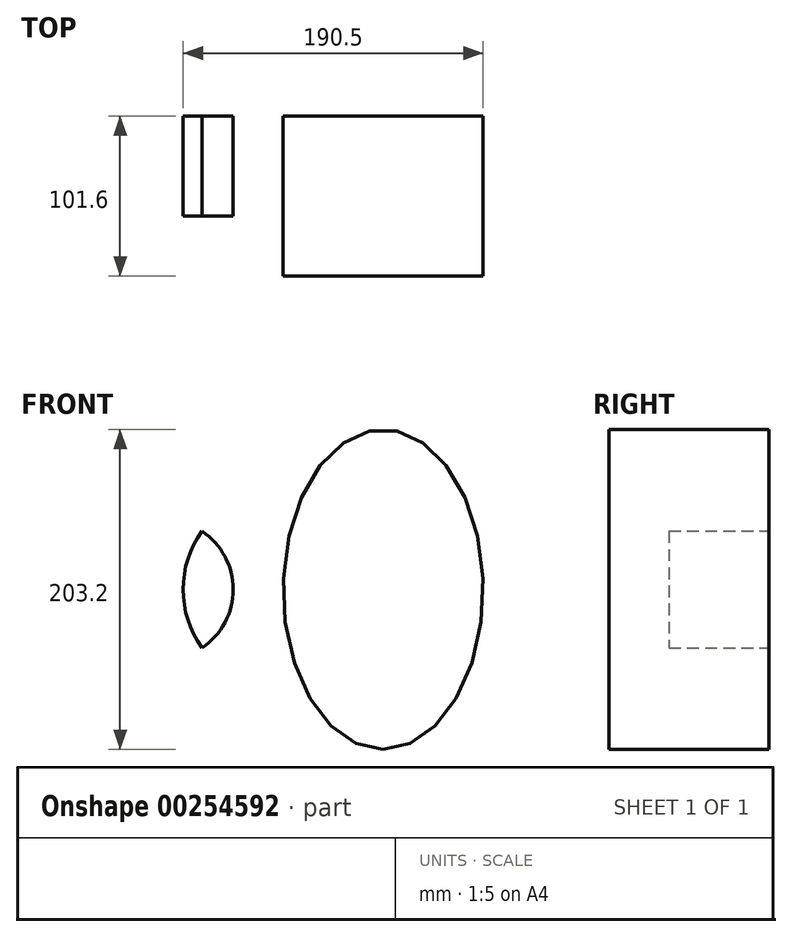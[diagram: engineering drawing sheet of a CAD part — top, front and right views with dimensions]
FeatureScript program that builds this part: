
annotation { "Feature Type Name" : "Feature", "Feature Type Description" : "" }
export const myFeature = defineFeature(function(context is Context, id is Id, definition is map)
    precondition{}
    {
        {
            var Q0;
            Q0=qCreatedBy(makeId("Front.planeOp"),FACE);
            var sketch = newSketch(context, id + "F0", { "sketchPlane" : qUnion([Q0])});
            skLineSegment(sketch, "E0", {"start": v(0, 0) * mm, "end": v(50.8, 0) * mm});
            skLineSegment(sketch, "E1", {"start": v(0, 0) * mm, "end": v(-76.2, 0) * mm});
            skCircle(sketch, "E2", {"center": v(-76.2, 0) * mm, "radius": 44.45 * mm});
            skLineSegment(sketch, "E3", {"start": v(-76.2, 0) * mm, "end": v(0, 0) * mm});
            skLineSegment(sketch, "E4", {"start": v(-31.75, 0) * mm, "end": v(-63.5, 0) * mm});
            skCircle(sketch, "E5", {"center": v(0, 0) * mm, "radius": 63.5 * mm});
            skPoint(sketch, "E6.orphan", {"position": v(50.8, 101.6) * mm});
            skEllipse(sketch, "E7", {"center": v(63.5, 0) * mm, "majorRadius": 63.5 * mm, "minorRadius": 101.6 * mm, "majorAxis": v(-1, 0)});
            skLineSegment(sketch, "E8", {"start": v(63.5, 0) * mm, "end": v(63.5, 101.6) * mm});
            skSolve(sketch);
        }
        {
            var Q0;
            {var subQ0=sQuery(id+"F0.wireOp",EDGE,"E5");var subQ1=sQuery(id+"F0.wireOp",EDGE,"E2");var subQ2=makeQuery(id+"F0.imprint","INTERSECT",VERTEX,{"disambiguationData":[OD(0.0)],"derivedFrom":[subQ1,subQ0]});Q0=makeQuery(id+"F0.imprint","IMPRINT",FACE,{"disambiguationData":[TD([[makeQuery(id+"F0.imprint","IMPRINT",EDGE,{"disambiguationData":[TD([[subQ2,-1.0]])],"derivedFrom":subQ1}),1.0]])]});}
            extrude(context, id + "F1", {"entities" : qUnion([Q0]), "depth" : 25.4 * mm});
        }
        {
            var Q0;
            {var subQ1=sQuery(id+"F0.wireOp",EDGE,"E2");var subQ3=sQuery(id+"F0.wireOp",EDGE,"E5");var subQ4=makeQuery(id+"F0.imprint","INTERSECT",VERTEX,{"disambiguationData":[OD(0.0)],"derivedFrom":[subQ1,subQ3]});Q0=makeQuery(id+"F0.imprint","IMPRINT",FACE,{"disambiguationData":[TD([[makeQuery(id+"F0.imprint","IMPRINT",EDGE,{"disambiguationData":[TD([[subQ4,1.0]])],"derivedFrom":subQ3}),1.0]])]});}
            var Q1;
            {var subQ0=sQuery(id+"F0.wireOp",EDGE,"E4");Q1=makeQuery(id+"F0.imprint","IMPRINT",FACE,{"disambiguationData":[TD([[makeQuery(id+"F0.imprint","IMPRINT",EDGE,{"derivedFrom":subQ0}),-1.0]])]});}
            var Q2;
            {var subQ0=sQuery(id+"F0.wireOp",EDGE,"E4");Q2=makeQuery(id+"F0.imprint","IMPRINT",FACE,{"disambiguationData":[TD([[makeQuery(id+"F0.imprint","IMPRINT",EDGE,{"derivedFrom":subQ0}),1.0]])]});}
            var Q3;
            {var subQ1=sQuery(id+"F0.wireOp",EDGE,"E2");var subQ3=sQuery(id+"F0.wireOp",EDGE,"E5");var subQ4=makeQuery(id+"F0.imprint","INTERSECT",VERTEX,{"disambiguationData":[OD(1.0)],"derivedFrom":[subQ1,subQ3]});Q3=makeQuery(id+"F0.imprint","IMPRINT",FACE,{"disambiguationData":[TD([[makeQuery(id+"F0.imprint","IMPRINT",EDGE,{"disambiguationData":[TD([[subQ4,-1.0]])],"derivedFrom":subQ3}),1.0]])]});}
            extrude(context, id + "F2", {"entities" : qUnion([Q0, Q1, Q2, Q3]), "operationType" : NewBodyOperationType.ADD, "depth" : 63.5 * mm});
        }
        {
            var Q0;
            {var subQ0=sQuery(id+"F0.wireOp",EDGE,"E8");Q0=makeQuery(id+"F0.imprint","IMPRINT",FACE,{"disambiguationData":[TD([[makeQuery(id+"F0.imprint","IMPRINT",EDGE,{"derivedFrom":subQ0}),1.0]])]});}
            var Q1;
            {var subQ0=sQuery(id+"F0.wireOp",EDGE,"E8");Q1=makeQuery(id+"F0.imprint","IMPRINT",FACE,{"disambiguationData":[TD([[makeQuery(id+"F0.imprint","IMPRINT",EDGE,{"derivedFrom":subQ0}),-1.0]])]});}
            var Q2;
            {var subQ0=sQuery(id+"F0.wireOp",EDGE,"E5");var subQ1=makeQuery(id+"F0.imprint","INTERSECT",VERTEX,{"derivedFrom":[subQ0,sQuery(id+"F0.wireOp",EDGE,"E8")]});Q2=makeQuery(id+"F0.imprint","IMPRINT",FACE,{"disambiguationData":[TD([[makeQuery(id+"F0.imprint","IMPRINT",EDGE,{"disambiguationData":[TD([[subQ1,-1.0]])],"derivedFrom":subQ0}),1.0]])]});}
            extrude(context, id + "F3", {"entities" : qUnion([Q0, Q1, Q2]), "operationType" : NewBodyOperationType.ADD, "depth" : 101.6 * mm});
        }
    });
